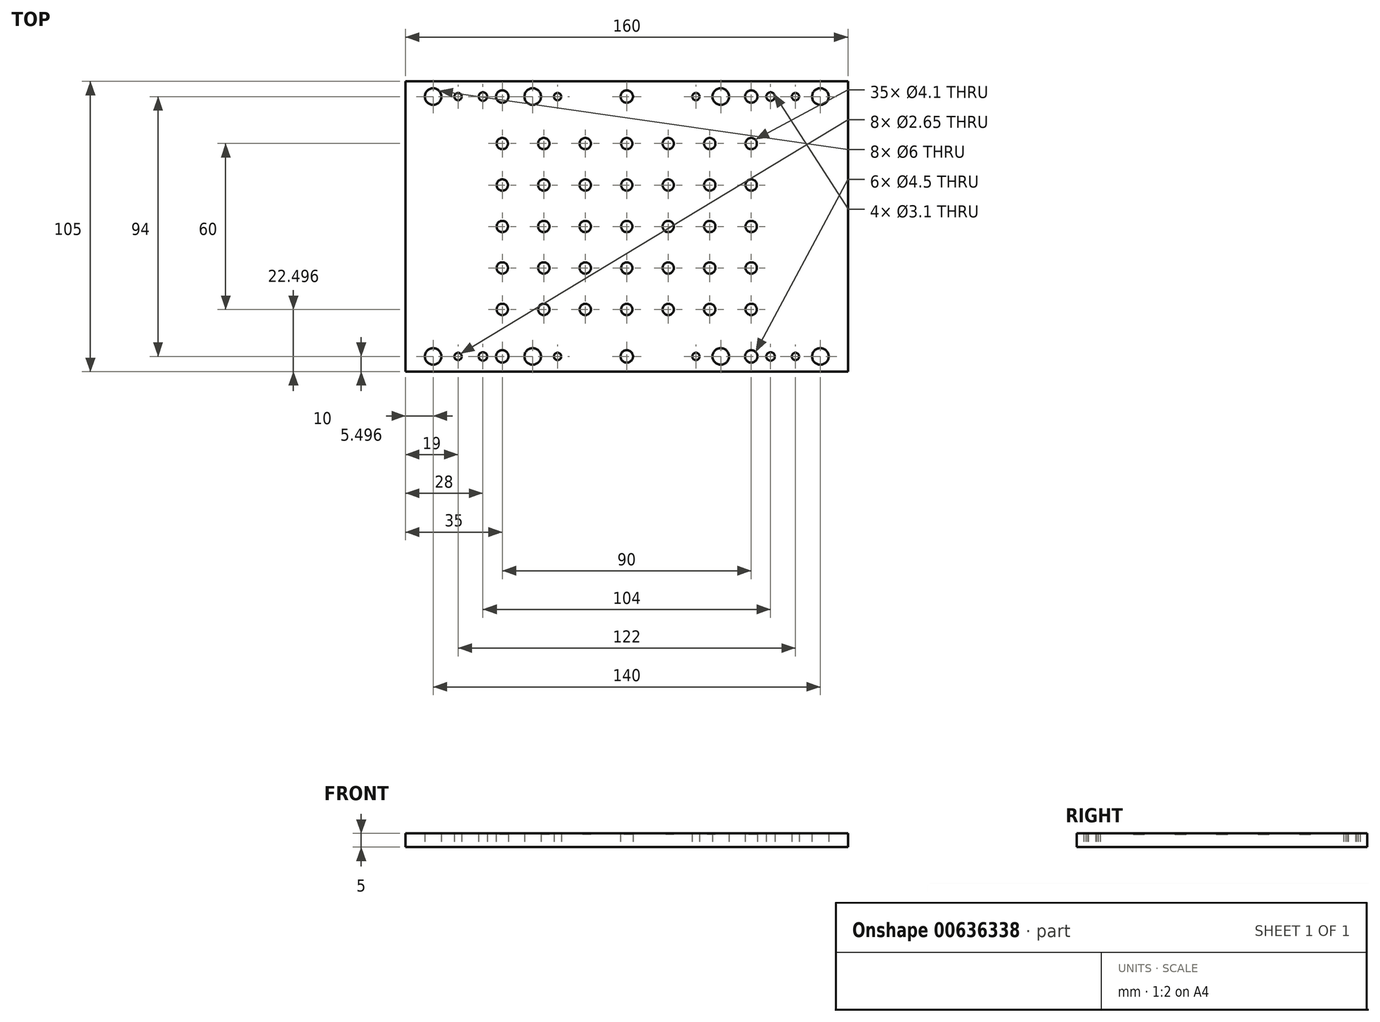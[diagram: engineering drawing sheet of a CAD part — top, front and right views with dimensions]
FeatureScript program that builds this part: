
annotation { "Feature Type Name" : "Feature", "Feature Type Description" : "" }
export const myFeature = defineFeature(function(context is Context, id is Id, definition is map)
    precondition{}
    {
        {
            var Q0;
            Q0=qCreatedBy(makeId("Top.planeOp"),FACE);
            var sketch = newSketch(context, id + "F0", { "sketchPlane" : qUnion([Q0])});
            skLineSegment(sketch, "E0.bottom", {"start": v(-90.54, 47.28) * mm, "end": v(69.46, 47.28) * mm});
            skLineSegment(sketch, "E0.top", {"start": v(-90.54, -57.72) * mm, "end": v(69.46, -57.72) * mm});
            skLineSegment(sketch, "E0.right", {"start": v(69.46, 47.28) * mm, "end": v(69.46, -57.72) * mm});
            skLineSegment(sketch, "E1", {"start": v(-90.54, -5.22) * mm, "end": v(69.46, -5.22) * mm, "construction": true});
            skCircle(sketch, "E2", {"center": v(-80.54, 41.78) * mm, "radius": 3 * mm});
            skCircle(sketch, "E3", {"center": v(-62.54, 41.78) * mm, "radius": 1.55 * mm});
            skCircle(sketch, "E4", {"center": v(-71.54, 41.78) * mm, "radius": 1.32 * mm});
            skCircle(sketch, "E5", {"center": v(-55.54, 41.78) * mm, "radius": 2.25 * mm});
            skCircle(sketch, "E6", {"center": v(-10.54, 41.78) * mm, "radius": 2.25 * mm});
            skCircle(sketch, "E7", {"center": v(-44.54, 41.78) * mm, "radius": 3 * mm});
            skCircle(sketch, "E8", {"center": v(-35.54, 41.78) * mm, "radius": 1.32 * mm});
            skCircle(sketch, "E9.MirrorC", {"center": v(50.46, 41.78) * mm, "radius": 1.32 * mm});
            skCircle(sketch, "E10.MirrorC", {"center": v(34.46, 41.78) * mm, "radius": 2.25 * mm});
            skCircle(sketch, "E11.MirrorC", {"center": v(14.46, 41.78) * mm, "radius": 1.32 * mm});
            skCircle(sketch, "E12.MirrorC", {"center": v(59.46, 41.78) * mm, "radius": 3 * mm});
            skCircle(sketch, "E13.MirrorC", {"center": v(41.46, 41.78) * mm, "radius": 1.55 * mm});
            skCircle(sketch, "E14.MirrorC", {"center": v(23.46, 41.78) * mm, "radius": 3 * mm});
            skCircle(sketch, "E15.MirrorC", {"center": v(59.46, -52.22) * mm, "radius": 3 * mm});
            skCircle(sketch, "E16.MirrorC", {"center": v(50.46, -52.22) * mm, "radius": 1.32 * mm});
            skCircle(sketch, "E17.MirrorC", {"center": v(41.46, -52.22) * mm, "radius": 1.55 * mm});
            skCircle(sketch, "E18.MirrorC", {"center": v(34.46, -52.22) * mm, "radius": 2.25 * mm});
            skCircle(sketch, "E19.MirrorC", {"center": v(23.46, -52.22) * mm, "radius": 3 * mm});
            skCircle(sketch, "E20.MirrorC", {"center": v(14.46, -52.22) * mm, "radius": 1.32 * mm});
            skCircle(sketch, "E21.MirrorC", {"center": v(-10.54, -52.22) * mm, "radius": 2.25 * mm});
            skCircle(sketch, "E22.MirrorC", {"center": v(-35.54, -52.22) * mm, "radius": 1.32 * mm});
            skCircle(sketch, "E23.MirrorC", {"center": v(-44.54, -52.22) * mm, "radius": 3 * mm});
            skCircle(sketch, "E24.MirrorC", {"center": v(-55.54, -52.22) * mm, "radius": 2.25 * mm});
            skCircle(sketch, "E25.MirrorC", {"center": v(-62.54, -52.22) * mm, "radius": 1.55 * mm});
            skCircle(sketch, "E26.MirrorC", {"center": v(-71.54, -52.22) * mm, "radius": 1.32 * mm});
            skCircle(sketch, "E27.MirrorC", {"center": v(-80.54, -52.22) * mm, "radius": 3 * mm});
            skLineSegment(sketch, "E28", {"start": v(-90.54, 47.28) * mm, "end": v(-90.54, -57.72) * mm});
            skCircle(sketch, "E29", {"center": v(-55.54, -35.22) * mm, "radius": 2.05 * mm});
            skCircle(sketch, "E30.0.1.0", {"center": v(-55.54, -20.22) * mm, "radius": 2.05 * mm});
            skCircle(sketch, "E30.0.2.0", {"center": v(-55.54, -5.22) * mm, "radius": 2.05 * mm});
            skCircle(sketch, "E30.0.3.0", {"center": v(-55.54, 9.78) * mm, "radius": 2.05 * mm});
            skCircle(sketch, "E30.0.4.0", {"center": v(-55.54, 24.78) * mm, "radius": 2.05 * mm});
            skCircle(sketch, "E30.1.0.0", {"center": v(-40.54, -35.22) * mm, "radius": 2.05 * mm});
            skCircle(sketch, "E30.1.1.0", {"center": v(-40.54, -20.22) * mm, "radius": 2.05 * mm});
            skCircle(sketch, "E30.1.2.0", {"center": v(-40.54, -5.22) * mm, "radius": 2.05 * mm});
            skCircle(sketch, "E30.1.3.0", {"center": v(-40.54, 9.78) * mm, "radius": 2.05 * mm});
            skCircle(sketch, "E30.1.4.0", {"center": v(-40.54, 24.78) * mm, "radius": 2.05 * mm});
            skCircle(sketch, "E30.2.0.0", {"center": v(-25.54, -35.22) * mm, "radius": 2.05 * mm});
            skCircle(sketch, "E30.2.1.0", {"center": v(-25.54, -20.22) * mm, "radius": 2.05 * mm});
            skCircle(sketch, "E30.2.2.0", {"center": v(-25.54, -5.22) * mm, "radius": 2.05 * mm});
            skCircle(sketch, "E30.2.3.0", {"center": v(-25.54, 9.78) * mm, "radius": 2.05 * mm});
            skCircle(sketch, "E30.2.4.0", {"center": v(-25.54, 24.78) * mm, "radius": 2.05 * mm});
            skCircle(sketch, "E30.3.0.0", {"center": v(-10.54, -35.22) * mm, "radius": 2.05 * mm});
            skCircle(sketch, "E30.3.1.0", {"center": v(-10.54, -20.22) * mm, "radius": 2.05 * mm});
            skCircle(sketch, "E30.3.2.0", {"center": v(-10.54, -5.22) * mm, "radius": 2.05 * mm});
            skCircle(sketch, "E30.3.3.0", {"center": v(-10.54, 9.78) * mm, "radius": 2.05 * mm});
            skCircle(sketch, "E30.3.4.0", {"center": v(-10.54, 24.78) * mm, "radius": 2.05 * mm});
            skCircle(sketch, "E30.4.0.0", {"center": v(4.46, -35.22) * mm, "radius": 2.05 * mm});
            skCircle(sketch, "E30.4.1.0", {"center": v(4.46, -20.22) * mm, "radius": 2.05 * mm});
            skCircle(sketch, "E30.4.2.0", {"center": v(4.46, -5.22) * mm, "radius": 2.05 * mm});
            skCircle(sketch, "E30.4.3.0", {"center": v(4.46, 9.78) * mm, "radius": 2.05 * mm});
            skCircle(sketch, "E30.4.4.0", {"center": v(4.46, 24.78) * mm, "radius": 2.05 * mm});
            skCircle(sketch, "E30.5.0.0", {"center": v(19.46, -35.22) * mm, "radius": 2.05 * mm});
            skCircle(sketch, "E30.5.1.0", {"center": v(19.46, -20.22) * mm, "radius": 2.05 * mm});
            skCircle(sketch, "E30.5.2.0", {"center": v(19.46, -5.22) * mm, "radius": 2.05 * mm});
            skCircle(sketch, "E30.5.3.0", {"center": v(19.46, 9.78) * mm, "radius": 2.05 * mm});
            skCircle(sketch, "E30.5.4.0", {"center": v(19.46, 24.78) * mm, "radius": 2.05 * mm});
            skCircle(sketch, "E30.6.0.0", {"center": v(34.46, -35.22) * mm, "radius": 2.05 * mm});
            skCircle(sketch, "E30.6.1.0", {"center": v(34.46, -20.22) * mm, "radius": 2.05 * mm});
            skCircle(sketch, "E30.6.2.0", {"center": v(34.46, -5.22) * mm, "radius": 2.05 * mm});
            skCircle(sketch, "E30.6.3.0", {"center": v(34.46, 9.78) * mm, "radius": 2.05 * mm});
            skCircle(sketch, "E30.6.4.0", {"center": v(34.46, 24.78) * mm, "radius": 2.05 * mm});
            skSolve(sketch);
        }
        {
            var Q0;
            Q0=sQuery(id+"F0.wireOp",EDGE,"E28");
            var Q1;
            Q1=sQuery(id+"F0.wireOp",EDGE,"E0.bottom");
            var Q2;
            Q2=sQuery(id+"F0.wireOp",EDGE,"E0.top");
            var Q3;
            Q3=sQuery(id+"F0.wireOp",EDGE,"E0.right");
            extrude(context, id + "F1", {"bodyType" : ToolBodyType.SURFACE, "surfaceEntities" : qUnion([Q0, Q1, Q2, Q3]), "oppositeDirection" : true, "depth" : 5 * mm, "offsetDistance" : 25 * mm});
        }
        {
            var Q0;
            Q0=sQuery(id+"F0.wireOp",EDGE,"E27.MirrorC");
            var Q1;
            Q1=sQuery(id+"F0.wireOp",EDGE,"E26.MirrorC");
            var Q2;
            Q2=sQuery(id+"F0.wireOp",EDGE,"E25.MirrorC");
            var Q3;
            Q3=sQuery(id+"F0.wireOp",EDGE,"E24.MirrorC");
            var Q4;
            Q4=sQuery(id+"F0.wireOp",EDGE,"E23.MirrorC");
            var Q5;
            Q5=sQuery(id+"F0.wireOp",EDGE,"E22.MirrorC");
            var Q6;
            Q6=sQuery(id+"F0.wireOp",EDGE,"E21.MirrorC");
            var Q7;
            Q7=sQuery(id+"F0.wireOp",EDGE,"E20.MirrorC");
            var Q8;
            Q8=sQuery(id+"F0.wireOp",EDGE,"E19.MirrorC");
            var Q9;
            Q9=sQuery(id+"F0.wireOp",EDGE,"E18.MirrorC");
            var Q10;
            Q10=sQuery(id+"F0.wireOp",EDGE,"E17.MirrorC");
            var Q11;
            Q11=sQuery(id+"F0.wireOp",EDGE,"E16.MirrorC");
            var Q12;
            Q12=sQuery(id+"F0.wireOp",EDGE,"E15.MirrorC");
            extrude(context, id + "F2", {"bodyType" : ToolBodyType.SURFACE, "surfaceEntities" : qUnion([Q0, Q1, Q2, Q3, Q4, Q5, Q6, Q7, Q8, Q9, Q10, Q11, Q12]), "oppositeDirection" : true, "depth" : 5 * mm, "offsetDistance" : 25 * mm});
        }
        {
            var Q0;
            Q0=sQuery(id+"F0.wireOp",EDGE,"E29");
            var Q1;
            Q1=sQuery(id+"F0.wireOp",EDGE,"E30.0.1.0");
            var Q2;
            Q2=sQuery(id+"F0.wireOp",EDGE,"E30.0.2.0");
            var Q3;
            Q3=sQuery(id+"F0.wireOp",EDGE,"E30.1.1.0");
            var Q4;
            Q4=sQuery(id+"F0.wireOp",EDGE,"E30.2.0.0");
            var Q5;
            Q5=sQuery(id+"F0.wireOp",EDGE,"E30.2.1.0");
            var Q6;
            Q6=sQuery(id+"F0.wireOp",EDGE,"E30.1.0.0");
            var Q7;
            Q7=sQuery(id+"F0.wireOp",EDGE,"E30.3.0.0");
            var Q8;
            Q8=sQuery(id+"F0.wireOp",EDGE,"E30.3.1.0");
            var Q9;
            Q9=sQuery(id+"F0.wireOp",EDGE,"E30.4.1.0");
            var Q10;
            Q10=sQuery(id+"F0.wireOp",EDGE,"E30.4.0.0");
            var Q11;
            Q11=sQuery(id+"F0.wireOp",EDGE,"E30.5.0.0");
            var Q12;
            Q12=sQuery(id+"F0.wireOp",EDGE,"E30.6.0.0");
            var Q13;
            Q13=sQuery(id+"F0.wireOp",EDGE,"E30.6.1.0");
            var Q14;
            Q14=sQuery(id+"F0.wireOp",EDGE,"E30.5.1.0");
            var Q15;
            Q15=sQuery(id+"F0.wireOp",EDGE,"E30.5.2.0");
            var Q16;
            Q16=sQuery(id+"F0.wireOp",EDGE,"E30.4.2.0");
            var Q17;
            Q17=sQuery(id+"F0.wireOp",EDGE,"E30.3.2.0");
            var Q18;
            Q18=sQuery(id+"F0.wireOp",EDGE,"E30.6.2.0");
            var Q19;
            Q19=sQuery(id+"F0.wireOp",EDGE,"E30.2.2.0");
            var Q20;
            Q20=sQuery(id+"F0.wireOp",EDGE,"E30.1.2.0");
            var Q21;
            Q21=sQuery(id+"F0.wireOp",EDGE,"E30.0.3.0");
            var Q22;
            Q22=sQuery(id+"F0.wireOp",EDGE,"E30.0.4.0");
            var Q23;
            Q23=sQuery(id+"F0.wireOp",EDGE,"E30.1.4.0");
            var Q24;
            Q24=sQuery(id+"F0.wireOp",EDGE,"E30.1.3.0");
            var Q25;
            Q25=sQuery(id+"F0.wireOp",EDGE,"E30.2.3.0");
            var Q26;
            Q26=sQuery(id+"F0.wireOp",EDGE,"E30.3.3.0");
            var Q27;
            Q27=sQuery(id+"F0.wireOp",EDGE,"E30.2.4.0");
            var Q28;
            Q28=sQuery(id+"F0.wireOp",EDGE,"E30.3.4.0");
            var Q29;
            Q29=sQuery(id+"F0.wireOp",EDGE,"E30.4.4.0");
            var Q30;
            Q30=sQuery(id+"F0.wireOp",EDGE,"E30.4.3.0");
            var Q31;
            Q31=sQuery(id+"F0.wireOp",EDGE,"E30.5.3.0");
            var Q32;
            Q32=sQuery(id+"F0.wireOp",EDGE,"E30.5.4.0");
            var Q33;
            Q33=sQuery(id+"F0.wireOp",EDGE,"E30.6.4.0");
            var Q34;
            Q34=sQuery(id+"F0.wireOp",EDGE,"E30.6.3.0");
            extrude(context, id + "F3", {"bodyType" : ToolBodyType.SURFACE, "surfaceEntities" : qUnion([Q0, Q1, Q2, Q3, Q4, Q5, Q6, Q7, Q8, Q9, Q10, Q11, Q12, Q13, Q14, Q15, Q16, Q17, Q18, Q19, Q20, Q21, Q22, Q23, Q24, Q25, Q26, Q27, Q28, Q29, Q30, Q31, Q32, Q33, Q34]), "oppositeDirection" : true, "depth" : 0.4 * mm, "offsetDistance" : 25 * mm});
        }
        {
            var Q0;
            Q0=sQuery(id+"F0.wireOp",EDGE,"E2");
            var Q1;
            Q1=sQuery(id+"F0.wireOp",EDGE,"E4");
            var Q2;
            Q2=sQuery(id+"F0.wireOp",EDGE,"E3");
            var Q3;
            Q3=sQuery(id+"F0.wireOp",EDGE,"E5");
            var Q4;
            Q4=sQuery(id+"F0.wireOp",EDGE,"E7");
            var Q5;
            Q5=sQuery(id+"F0.wireOp",EDGE,"E8");
            var Q6;
            Q6=sQuery(id+"F0.wireOp",EDGE,"E6");
            var Q7;
            Q7=sQuery(id+"F0.wireOp",EDGE,"E11.MirrorC");
            var Q8;
            Q8=sQuery(id+"F0.wireOp",EDGE,"E14.MirrorC");
            var Q9;
            Q9=sQuery(id+"F0.wireOp",EDGE,"E10.MirrorC");
            var Q10;
            Q10=sQuery(id+"F0.wireOp",EDGE,"E13.MirrorC");
            var Q11;
            Q11=sQuery(id+"F0.wireOp",EDGE,"E9.MirrorC");
            var Q12;
            Q12=sQuery(id+"F0.wireOp",EDGE,"E12.MirrorC");
            extrude(context, id + "F4", {"bodyType" : ToolBodyType.SURFACE, "surfaceEntities" : qUnion([Q0, Q1, Q2, Q3, Q4, Q5, Q6, Q7, Q8, Q9, Q10, Q11, Q12]), "oppositeDirection" : true, "depth" : 5 * mm, "offsetDistance" : 25 * mm});
        }
    });
